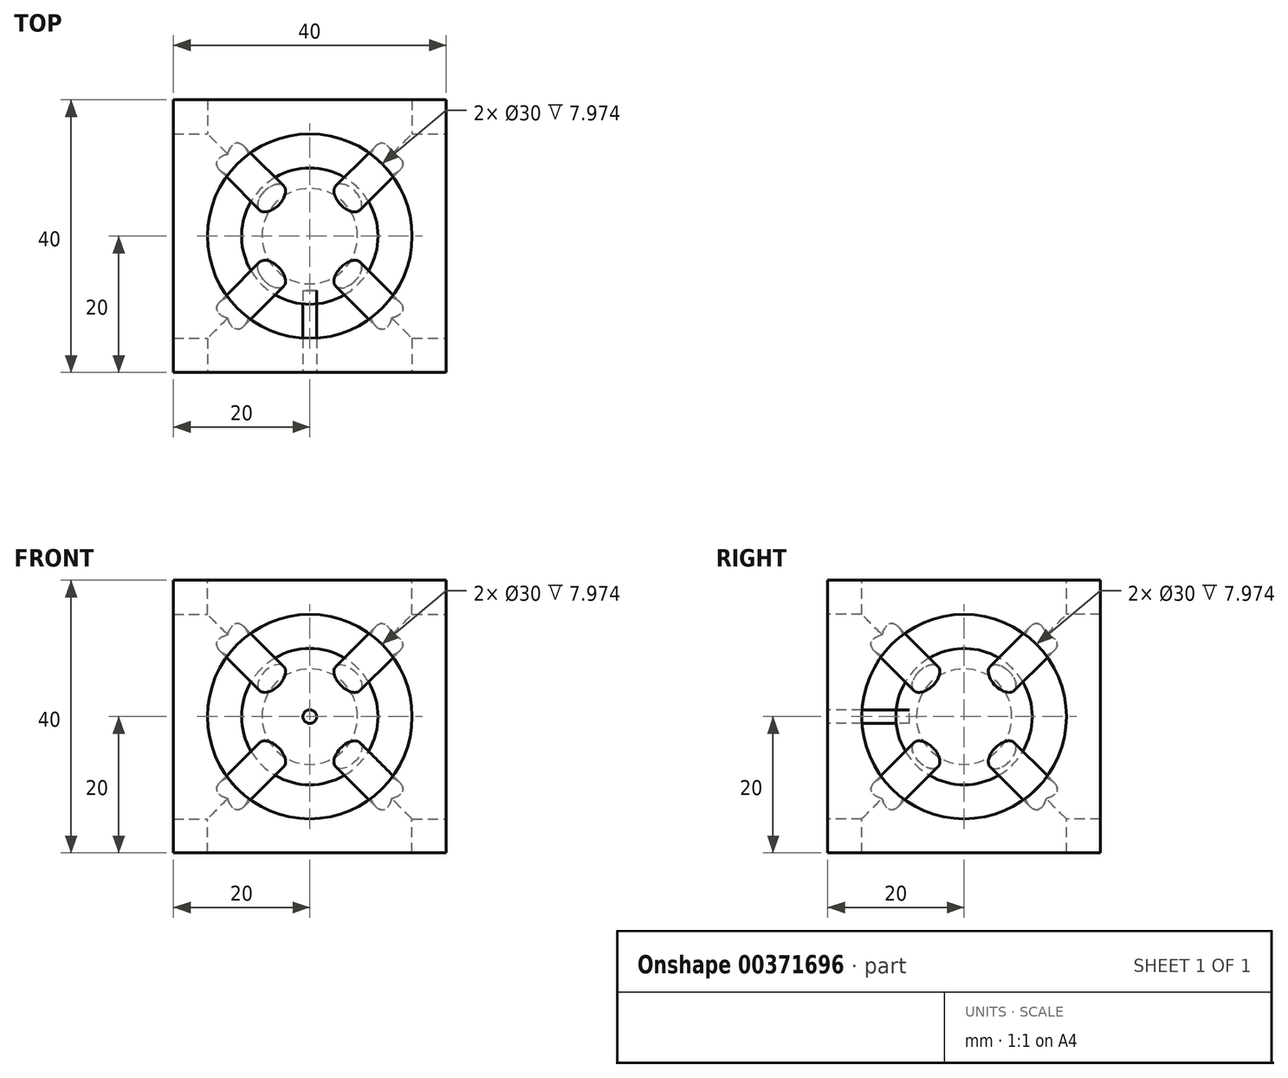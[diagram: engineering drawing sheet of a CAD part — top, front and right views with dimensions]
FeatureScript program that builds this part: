
annotation { "Feature Type Name" : "Feature", "Feature Type Description" : "" }
export const myFeature = defineFeature(function(context is Context, id is Id, definition is map)
    precondition{}
    {
        {
            var Q0;
            Q0=qCreatedBy(makeId("Top.planeOp"),FACE);
            var sketch = newSketch(context, id + "F0", { "sketchPlane" : qUnion([Q0])});
            skLineSegment(sketch, "E0.bottom", {"start": v(0, 0) * mm, "end": v(40, 0) * mm});
            skLineSegment(sketch, "E0.top", {"start": v(0, 40) * mm, "end": v(40, 40) * mm});
            skLineSegment(sketch, "E0.left", {"start": v(0, 0) * mm, "end": v(0, 40) * mm});
            skLineSegment(sketch, "E0.right", {"start": v(40, 0) * mm, "end": v(40, 40) * mm});
            skSolve(sketch);
        }
        {
            var Q0;
            Q0 = qSketchRegion(id + "F0", true);
            extrude(context, id + "F1", {"entities" : qUnion([Q0]), "depth" : 40 * mm});
        }
        {
            var Q0;
            Q0=makeQuery(id+"F1.opExtrude","SWEPT_FACE",FACE,{"disambiguationData":[OSD([sQuery(id+"F0.wireOp",EDGE,"E0.bottom")])]});
            var sketch = newSketch(context, id + "F2", { "sketchPlane" : qUnion([Q0])});
            skLineSegment(sketch, "E1", {"start": v(0, 0) * mm, "end": v(40, 40) * mm});
            skCircle(sketch, "E2", {"center": v(20, 20) * mm, "radius": 15 * mm});
            skSolve(sketch);
        }
        {
            var Q0;
            Q0 = qSketchRegion(id + "F2", true);
            extrude(context, id + "F3", {"entities" : qUnion([Q0]), "operationType" : NewBodyOperationType.REMOVE, "oppositeDirection" : true, "depth" : 40 * mm});
        }
        {
            var Q0;
            Q0=makeQuery(id+"F1.opExtrude","SWEPT_FACE",FACE,{"disambiguationData":[OSD([sQuery(id+"F0.wireOp",EDGE,"E0.right")])]});
            var sketch = newSketch(context, id + "F4", { "sketchPlane" : qUnion([Q0])});
            skLineSegment(sketch, "E3", {"start": v(0, 0) * mm, "end": v(40, 40) * mm});
            skCircle(sketch, "E4", {"center": v(20, 20) * mm, "radius": 15 * mm});
            skSolve(sketch);
        }
        {
            var Q0;
            Q0 = qSketchRegion(id + "F4", true);
            extrude(context, id + "F5", {"entities" : qUnion([Q0]), "operationType" : NewBodyOperationType.REMOVE, "oppositeDirection" : true, "depth" : 40 * mm});
        }
        {
            var Q0;
            Q0=makeQuery(id+"F1.opExtrude","CAP_FACE",FACE,{"disambiguationData":[OSD([sQuery(id+"F0.wireOp",EDGE,"E0.bottom"),sQuery(id+"F0.wireOp",EDGE,"E0.top"),sQuery(id+"F0.wireOp",EDGE,"E0.left"),sQuery(id+"F0.wireOp",EDGE,"E0.right")])],"isStart":false});
            var sketch = newSketch(context, id + "F6", { "sketchPlane" : qUnion([Q0])});
            skLineSegment(sketch, "E5", {"start": v(40, 40) * mm, "end": v(0, 0) * mm});
            skCircle(sketch, "E6", {"center": v(20, 20) * mm, "radius": 15 * mm});
            skSolve(sketch);
        }
        {
            var Q0;
            Q0 = qSketchRegion(id + "F6", true);
            extrude(context, id + "F7", {"entities" : qUnion([Q0]), "operationType" : NewBodyOperationType.REMOVE, "oppositeDirection" : true, "depth" : 40 * mm});
        }
        {
            var Q0;
            Q0=makeQuery(id+"F1.opExtrude","CAP_VERTEX",VERTEX,{"disambiguationData":[OSD([sQuery(id+"F0.wireOp",EDGE,"E0.bottom"),sQuery(id+"F0.wireOp",EDGE,"E0.right")])],"isStart":false});
            var Q1;
            Q1=makeQuery(id+"F1.opExtrude","CAP_VERTEX",VERTEX,{"disambiguationData":[OSD([sQuery(id+"F0.wireOp",EDGE,"E0.top"),sQuery(id+"F0.wireOp",EDGE,"E0.left")])],"isStart":true});
            var Q2;
            Q2=makeQuery(id+"F1.opExtrude","CAP_VERTEX",VERTEX,{"disambiguationData":[OSD([sQuery(id+"F0.wireOp",EDGE,"E0.top"),sQuery(id+"F0.wireOp",EDGE,"E0.left")])],"isStart":false});
            cPlane(context, id + "F8", {"entities" : qUnion([Q0, Q1, Q2]), "cplaneType" : CPlaneType.THREE_POINT, "offset" : 25 * mm, "width" : 150 * mm, "height" : 150 * mm});
        }
        {
            var Q0;
            Q0=qCreatedBy(id+"F8.planeOp",FACE);
            var sketch = newSketch(context, id + "F9", { "sketchPlane" : qUnion([Q0])});
            skPoint(sketch, "E7.0", {"position": v(28.28, 40) * mm});
            skPoint(sketch, "E8.0", {"position": v(-28.28, 0) * mm});
            skLineSegment(sketch, "E9", {"start": v(28.28, 40) * mm, "end": v(-28.28, 0) * mm});
            skLineSegment(sketch, "E10.0", {"start": v(26.84, 42.04) * mm, "end": v(-29.73, 2.04) * mm});
            skLineSegment(sketch, "E11", {"start": v(-22.58, 4.03) * mm, "end": v(-24.02, 6.07) * mm});
            skLineSegment(sketch, "E12", {"start": v(21.94, 35.51) * mm, "end": v(20.5, 37.55) * mm});
            skSolve(sketch);
        }
        {
            var Q0;
            {var subQ0=sQuery(id+"F9.wireOp",EDGE,"E11");Q0=makeQuery(id+"F9.imprint","IMPRINT",FACE,{"disambiguationData":[TD([[makeQuery(id+"F9.imprint","IMPRINT",EDGE,{"derivedFrom":subQ0}),-1.0]])]});}
            var Q1;
            Q1=sQuery(id+"F9.wireOp",EDGE,"E9");
            revolve(context, id + "F10", {"operationType" : NewBodyOperationType.ADD, "entities" : qUnion([Q0]), "axis" : qUnion([Q1]), "revolveType" : RevolveType.FULL});
        }
        {
            var Q0;
            Q0=qCreatedBy(id+"F8.planeOp",FACE);
            var sketch = newSketch(context, id + "F11", { "sketchPlane" : qUnion([Q0])});
            skPoint(sketch, "E13.0", {"position": v(28.28, 0) * mm});
            skPoint(sketch, "E14.0", {"position": v(-28.28, 40) * mm});
            skLineSegment(sketch, "E15", {"start": v(-28.28, 40) * mm, "end": v(28.28, 0) * mm});
            skLineSegment(sketch, "E16.0", {"start": v(-29.73, 37.96) * mm, "end": v(26.84, -2.04) * mm});
            skLineSegment(sketch, "E17", {"start": v(-24.87, 34.52) * mm, "end": v(-23.43, 36.56) * mm});
            skLineSegment(sketch, "E18", {"start": v(22.77, 0.84) * mm, "end": v(24.21, 2.88) * mm});
            skSolve(sketch);
        }
        {
            var Q0;
            {var subQ0=sQuery(id+"F11.wireOp",EDGE,"E17");Q0=makeQuery(id+"F11.imprint","IMPRINT",FACE,{"disambiguationData":[TD([[makeQuery(id+"F11.imprint","IMPRINT",EDGE,{"derivedFrom":subQ0}),-1.0]])]});}
            var Q1;
            Q1=sQuery(id+"F11.wireOp",EDGE,"E15");
            revolve(context, id + "F12", {"operationType" : NewBodyOperationType.ADD, "entities" : qUnion([Q0]), "axis" : qUnion([Q1]), "revolveType" : RevolveType.FULL});
        }
        {
            var Q0;
            Q0=makeQuery(id+"F1.opExtrude","CAP_VERTEX",VERTEX,{"disambiguationData":[OSD([sQuery(id+"F0.wireOp",EDGE,"E0.bottom"),sQuery(id+"F0.wireOp",EDGE,"E0.left")])],"isStart":false});
            var Q1;
            Q1=makeQuery(id+"F1.opExtrude","CAP_VERTEX",VERTEX,{"disambiguationData":[OSD([sQuery(id+"F0.wireOp",EDGE,"E0.top"),sQuery(id+"F0.wireOp",EDGE,"E0.right")])],"isStart":true});
            var Q2;
            Q2=makeQuery(id+"F1.opExtrude","CAP_VERTEX",VERTEX,{"disambiguationData":[OSD([sQuery(id+"F0.wireOp",EDGE,"E0.top"),sQuery(id+"F0.wireOp",EDGE,"E0.left")])],"isStart":true});
            cPlane(context, id + "F13", {"entities" : qUnion([Q0, Q1, Q2]), "cplaneType" : CPlaneType.THREE_POINT, "offset" : 25 * mm, "width" : 150 * mm, "height" : 150 * mm});
        }
        {
            var Q0;
            Q0=qCreatedBy(id+"F13.planeOp",FACE);
            var sketch = newSketch(context, id + "F14", { "sketchPlane" : qUnion([Q0])});
            skPoint(sketch, "E19.0", {"position": v(0, 28.28) * mm});
            skPoint(sketch, "E20.0", {"position": v(40, -28.28) * mm});
            skLineSegment(sketch, "E21", {"start": v(0, 28.28) * mm, "end": v(40, -28.28) * mm});
            skLineSegment(sketch, "E22.0", {"start": v(-2.04, 26.84) * mm, "end": v(37.96, -29.73) * mm});
            skLineSegment(sketch, "E23", {"start": v(1.24, 22.2) * mm, "end": v(2.2, 25.17) * mm});
            skLineSegment(sketch, "E24", {"start": v(34.84, -25.32) * mm, "end": v(36.88, -23.87) * mm});
            skSolve(sketch);
        }
        {
            var Q0;
            {var subQ0=sQuery(id+"F14.wireOp",EDGE,"E23");Q0=makeQuery(id+"F14.imprint","IMPRINT",FACE,{"disambiguationData":[TD([[makeQuery(id+"F14.imprint","IMPRINT",EDGE,{"derivedFrom":subQ0}),-1.0]])]});}
            var Q1;
            Q1=sQuery(id+"F14.wireOp",EDGE,"E21");
            revolve(context, id + "F15", {"operationType" : NewBodyOperationType.ADD, "entities" : qUnion([Q0]), "axis" : qUnion([Q1]), "revolveType" : RevolveType.FULL});
        }
        {
            var Q0;
            Q0=qCreatedBy(makeId("Origin.pointOp"),VERTEX);
            var Q1;
            Q1=makeQuery(id+"F1.opExtrude","CAP_VERTEX",VERTEX,{"disambiguationData":[OSD([sQuery(id+"F0.wireOp",EDGE,"E0.top"),sQuery(id+"F0.wireOp",EDGE,"E0.right")])],"isStart":false});
            var Q2;
            Q2=makeQuery(id+"F1.opExtrude","CAP_VERTEX",VERTEX,{"disambiguationData":[OSD([sQuery(id+"F0.wireOp",EDGE,"E0.bottom"),sQuery(id+"F0.wireOp",EDGE,"E0.right")])],"isStart":false});
            cPlane(context, id + "F16", {"entities" : qUnion([Q0, Q1, Q2]), "cplaneType" : CPlaneType.THREE_POINT, "offset" : 25 * mm, "width" : 150 * mm, "height" : 150 * mm});
        }
        {
            var Q0;
            Q0=qCreatedBy(id+"F16.planeOp",FACE);
            var sketch = newSketch(context, id + "F17", { "sketchPlane" : qUnion([Q0])});
            skLineSegment(sketch, "E25.0", {"start": v(0, 0) * mm, "end": v(-40, 0) * mm});
            skPoint(sketch, "E26.0", {"position": v(-40, 56.57) * mm});
            skLineSegment(sketch, "E27", {"start": v(0, 0) * mm, "end": v(-40, 56.57) * mm});
            skLineSegment(sketch, "E28.0", {"start": v(2.04, 1.44) * mm, "end": v(-37.96, 58.01) * mm});
            skLineSegment(sketch, "E29", {"start": v(-1.66, 2.35) * mm, "end": v(0, 4.33) * mm});
            skLineSegment(sketch, "E30", {"start": v(-34.96, 53.78) * mm, "end": v(-37, 52.33) * mm});
            skSolve(sketch);
        }
        {
            var Q0;
            {var subQ0=sQuery(id+"F17.wireOp",EDGE,"E29");Q0=makeQuery(id+"F17.imprint","IMPRINT",FACE,{"disambiguationData":[TD([[makeQuery(id+"F17.imprint","IMPRINT",EDGE,{"derivedFrom":subQ0}),1.0]])]});}
            var Q1;
            Q1=sQuery(id+"F17.wireOp",EDGE,"E27");
            revolve(context, id + "F18", {"operationType" : NewBodyOperationType.ADD, "entities" : qUnion([Q0]), "axis" : qUnion([Q1]), "revolveType" : RevolveType.FULL});
        }
        {
            var Q0;
            Q0=qCreatedBy(id+"F16.planeOp",FACE);
            var sketch = newSketch(context, id + "F19", { "sketchPlane" : qUnion([Q0])});
            skPoint(sketch, "E31.0", {"position": v(-40, 56.57) * mm});
            skPoint(sketch, "E32.0", {"position": v(0, 0) * mm});
            skLineSegment(sketch, "E33", {"start": v(-40, 56.57) * mm, "end": v(0, 0) * mm});
            skArc(sketch, "E34", {"start": v(-14.23, 20.12) * mm, "mid": v(-11.84, 34.06) * mm, "end": v(-25.77, 36.45) * mm});
            skSolve(sketch);
        }
        {
            var Q0;
            Q0 = qSketchRegion(id + "F19", true);
            var Q1;
            Q1=sQuery(id+"F19.wireOp",EDGE,"E33");
            revolve(context, id + "F20", {"operationType" : NewBodyOperationType.ADD, "entities" : qUnion([Q0]), "axis" : qUnion([Q1]), "revolveType" : RevolveType.FULL});
        }
        {
            var Q0;
            Q0=qCreatedBy(id+"F16.planeOp",FACE);
            var sketch = newSketch(context, id + "F21", { "sketchPlane" : qUnion([Q0])});
            skPoint(sketch, "E35.0", {"position": v(-40, 56.57) * mm});
            skPoint(sketch, "E36.0", {"position": v(0, 0) * mm});
            skLineSegment(sketch, "E37", {"start": v(-40, 56.57) * mm, "end": v(0, 0) * mm});
            skArc(sketch, "E38", {"start": v(-15.96, 22.57) * mm, "mid": v(-25.72, 24.24) * mm, "end": v(-24.04, 34) * mm});
            skSolve(sketch);
        }
        {
            var Q0;
            Q0 = qSketchRegion(id + "F21", true);
            var Q1;
            Q1=sQuery(id+"F21.wireOp",EDGE,"E37");
            revolve(context, id + "F22", {"operationType" : NewBodyOperationType.REMOVE, "entities" : qUnion([Q0]), "axis" : qUnion([Q1]), "revolveType" : RevolveType.FULL, "oppositeDirection" : true});
        }
        {
            var Q0;
            Q0=makeQuery(id+"F1.opExtrude","SWEPT_FACE",FACE,{"disambiguationData":[OSD([sQuery(id+"F0.wireOp",EDGE,"E0.bottom")])]});
            var sketch = newSketch(context, id + "F23", { "sketchPlane" : qUnion([Q0])});
            skLineSegment(sketch, "E39.0.0", {"start": v(0, 0) * mm, "end": v(40, 0) * mm});
            skLineSegment(sketch, "E39.0.1", {"start": v(40, 0) * mm, "end": v(40, 40) * mm});
            skLineSegment(sketch, "E39.0.2", {"start": v(40, 40) * mm, "end": v(0, 40) * mm});
            skLineSegment(sketch, "E39.0.3", {"start": v(0, 40) * mm, "end": v(0, 0) * mm});
            skCircle(sketch, "E40", {"center": v(20, 20) * mm, "radius": 1 * mm});
            skSolve(sketch);
        }
        {
            var Q0;
            Q0=makeQuery(id+"F23.imprint","IMPRINT",FACE,{"disambiguationData":[TD([[makeQuery(id+"F23.imprint","IMPRINT",EDGE,{"derivedFrom":sQuery(id+"F23.wireOp",EDGE,"E40")}),1.0]])]});
            extrude(context, id + "F24", {"entities" : qUnion([Q0]), "oppositeDirection" : true, "depth" : 12 * mm});
        }
    });
